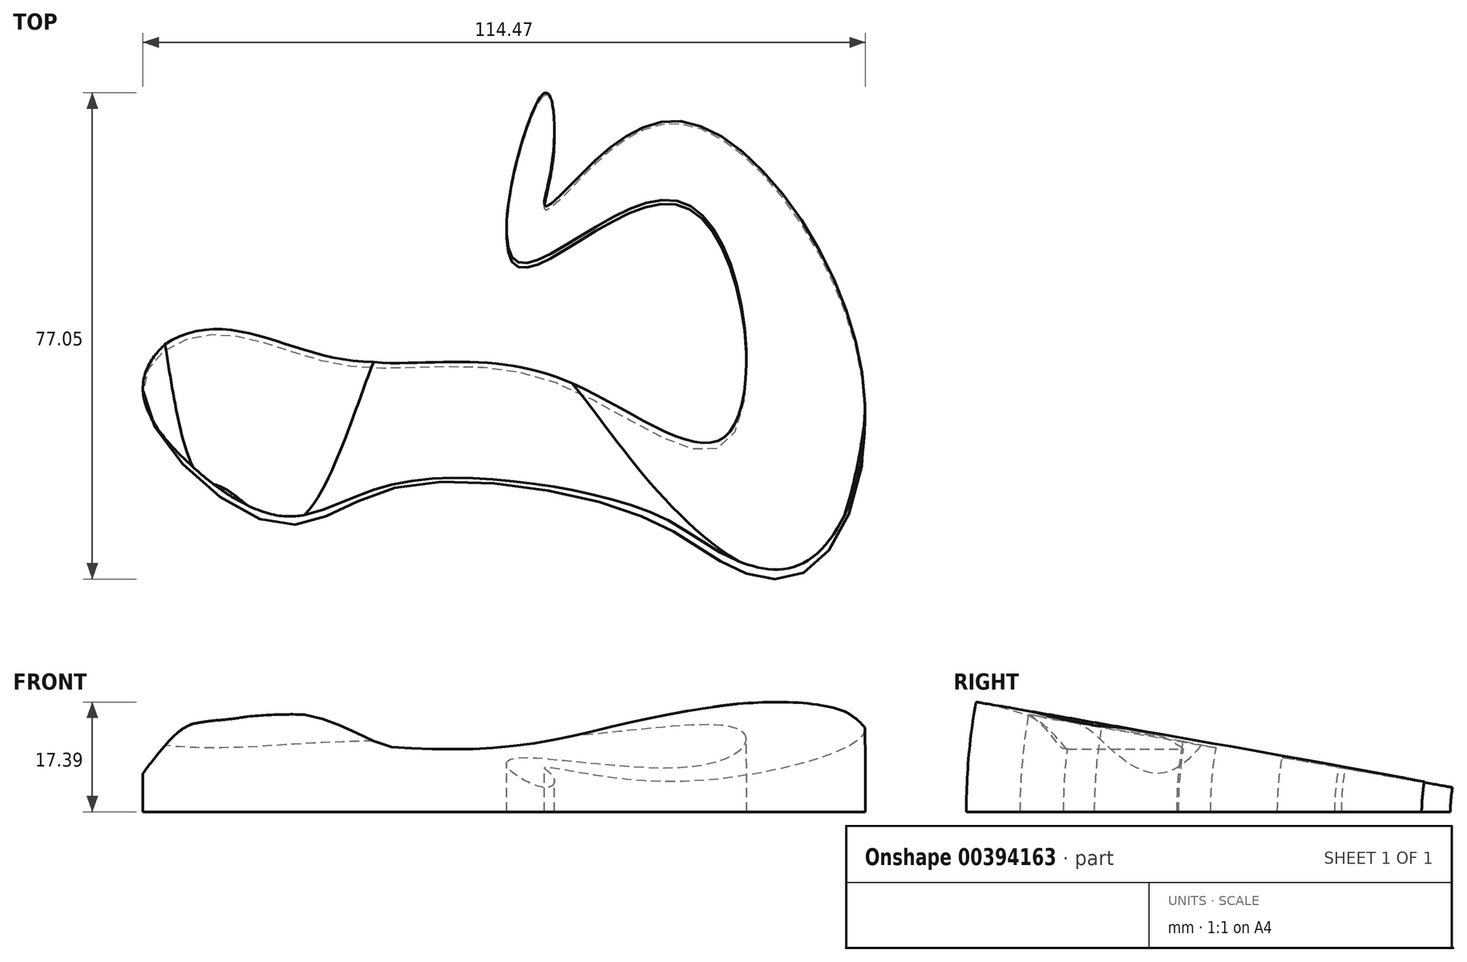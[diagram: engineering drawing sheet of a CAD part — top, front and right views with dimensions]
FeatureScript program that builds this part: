
annotation { "Feature Type Name" : "Feature", "Feature Type Description" : "" }
export const myFeature = defineFeature(function(context is Context, id is Id, definition is map)
    precondition{}
    {
        {
            var Q0;
            Q0=qCreatedBy(makeId("Top.planeOp"),FACE);
            var sketch = newSketch(context, id + "F0", { "sketchPlane" : qUnion([Q0])});
            skFitSpline(sketch, "E0", {"points": [v(23.71, 4.55) * mm, v(19.09, -22.23) * mm, v(45.45, -12.85) * mm, v(53.07, -50.09) * mm, v(25.01, -40.72) * mm, v(-7.44, -38.28) * mm, v(-29.28, -33.35) * mm, v(-39.8, -42.34) * mm, v(-18.98, -63.2) * mm, v(0, -57.63) * mm, v(39.63, -62.23) * mm, v(52.25, -69.55) * mm, v(65.09, -70.9) * mm, v(73.93, -38.78) * mm, v(46.05, 0) * mm, v(28.8, -9.32) * mm, v(23.95, -13.58) * mm, v(25.17, -5.57) * mm, v(23.71, 4.55) * mm]});
            skSolve(sketch);
        }
        {
            var Q0;
            Q0=makeQuery(id+"F0.imprint","IMPRINT",FACE,{"disambiguationData":[TD([[makeQuery(id+"F0.imprint","IMPRINT",EDGE,{"derivedFrom":sQuery(id+"F0.wireOp",EDGE,"E0")}),1.0]])]});
            var sketch = newSketch(context, id + "F1", { "sketchPlane" : qUnion([Q0])});
            skLineSegment(sketch, "E1", {"start": v(83.28, 28.97) * mm, "end": v(-35.27, 24.85) * mm, "construction": true});
            skSolve(sketch);
        }
        {
            var Q0;
            Q0=makeQuery(id+"F0.imprint","IMPRINT",FACE,{"disambiguationData":[TD([[makeQuery(id+"F0.imprint","IMPRINT",EDGE,{"derivedFrom":sQuery(id+"F0.wireOp",EDGE,"E0")}),1.0]])]});
            var Q1;
            Q1=sQuery(id+"F0.wireOp",EDGE,"E0");
            var Q2;
            Q2=sQuery(id+"F1.wireOp",EDGE,"E1");
            revolve(context, id + "F2", {"entities" : qUnion([Q0]), "surfaceEntities" : qUnion([Q1]), "axis" : qUnion([Q2]), "revolveType" : RevolveType.TWO_DIRECTIONS, "angle" : 10 * degree, "angleBack" : 0 * degree});
        }
        {
            var Q0;
            Q0=qCreatedBy(makeId("Front.planeOp"),FACE);
            var sketch = newSketch(context, id + "F3", { "sketchPlane" : qUnion([Q0])});
            skLineSegment(sketch, "E2", {"start": v(-54.59, -5.32) * mm, "end": v(80.6, -5.32) * mm});
            skFitSpline(sketch, "E3", {"points": [v(-54.59, -5.32) * mm, v(-44.93, 0) * mm, v(-33.7, 13) * mm, v(-27, 14.58) * mm, v(-14, 15.37) * mm, v(-2.36, 10.84) * mm, v(2.56, 10.05) * mm, v(14.39, 10.05) * mm, v(27.4, 11.82) * mm, v(41.19, 14.98) * mm, v(64.05, 17.54) * mm, v(74.69, 13.2) * mm, v(80.6, -5.32) * mm], "startDerivative": vector(125.5, 44.06) * mm, "endDerivative": vector(40.18, -212.48) * mm});
            skLineSegment(sketch, "E4.bottom", {"start": v(-63.26, 38.23) * mm, "end": v(88.48, 38.23) * mm});
            skLineSegment(sketch, "E4.top", {"start": v(-63.26, -11.23) * mm, "end": v(88.48, -11.23) * mm});
            skLineSegment(sketch, "E4.left", {"start": v(-63.26, 38.23) * mm, "end": v(-63.26, -11.23) * mm});
            skLineSegment(sketch, "E4.right", {"start": v(88.48, 38.23) * mm, "end": v(88.48, -11.23) * mm});
            skSolve(sketch);
        }
        {
            var Q0;
            Q0 = qSketchRegion(id + "F3", true);
            extrude(context, id + "F4", {"entities" : qUnion([Q0]), "operationType" : NewBodyOperationType.REMOVE, "depth" : 76.2 * mm});
        }
    });
